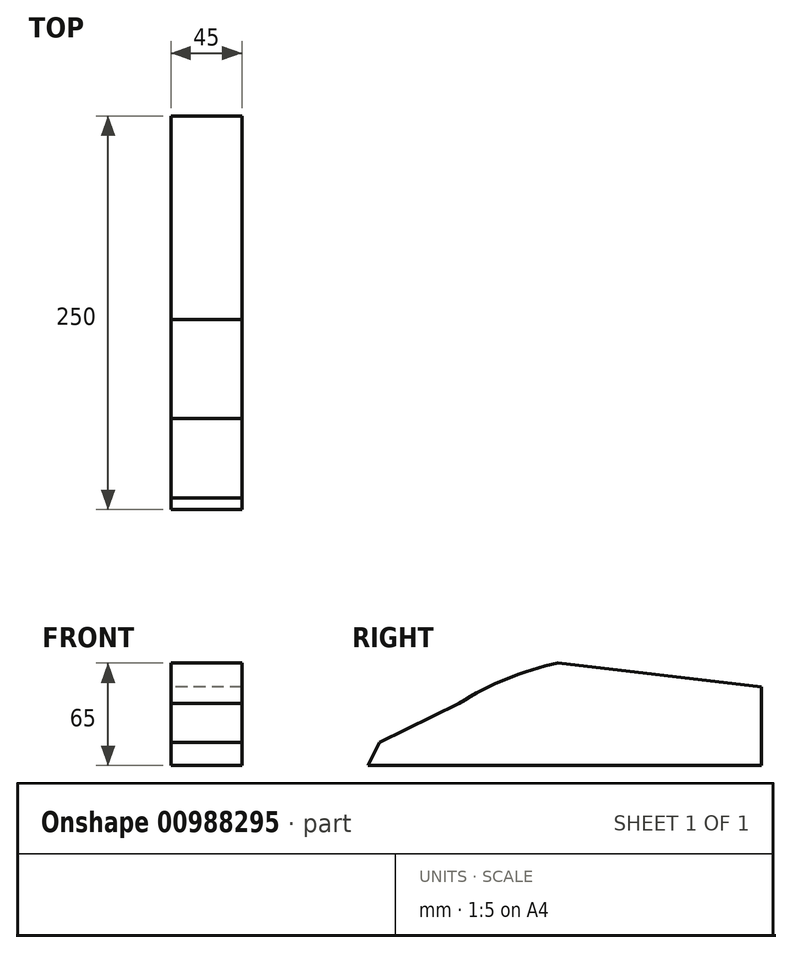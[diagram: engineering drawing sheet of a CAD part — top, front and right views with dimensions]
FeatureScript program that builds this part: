
annotation { "Feature Type Name" : "Feature", "Feature Type Description" : "" }
export const myFeature = defineFeature(function(context is Context, id is Id, definition is map)
    precondition{}
    {
        {
            var Q0;
            Q0=qCreatedBy(makeId("Right.planeOp"),FACE);
            var sketch = newSketch(context, id + "F0", { "sketchPlane" : qUnion([Q0])});
            skLineSegment(sketch, "E0", {"start": v(0, 0) * mm, "end": v(250, 0) * mm});
            skLineSegment(sketch, "E1", {"start": v(250, 0) * mm, "end": v(250, 50) * mm});
            skLineSegment(sketch, "E2", {"start": v(250, 50) * mm, "end": v(120.87, 65) * mm});
            skArc(sketch, "E3", {"start": v(120.87, 65) * mm, "mid": v(88.26, 55.06) * mm, "end": v(58, 39.38) * mm});
            skLineSegment(sketch, "E4", {"start": v(0, 0) * mm, "end": v(7.45, 14.54) * mm});
            skLineSegment(sketch, "E5", {"start": v(7.45, 14.54) * mm, "end": v(58, 39.38) * mm});
            skSolve(sketch);
        }
        {
            var Q0;
            Q0=makeQuery(id+"F0.imprint","IMPRINT",FACE,{"disambiguationData":[TD([[makeQuery(id+"F0.imprint","IMPRINT",EDGE,{"derivedFrom":sQuery(id+"F0.wireOp",EDGE,"E0")}),1.0]])]});
            extrude(context, id + "F1", {"entities" : qUnion([Q0]), "depth" : 45 * mm, "offsetDistance" : 25 * mm});
        }
    });
